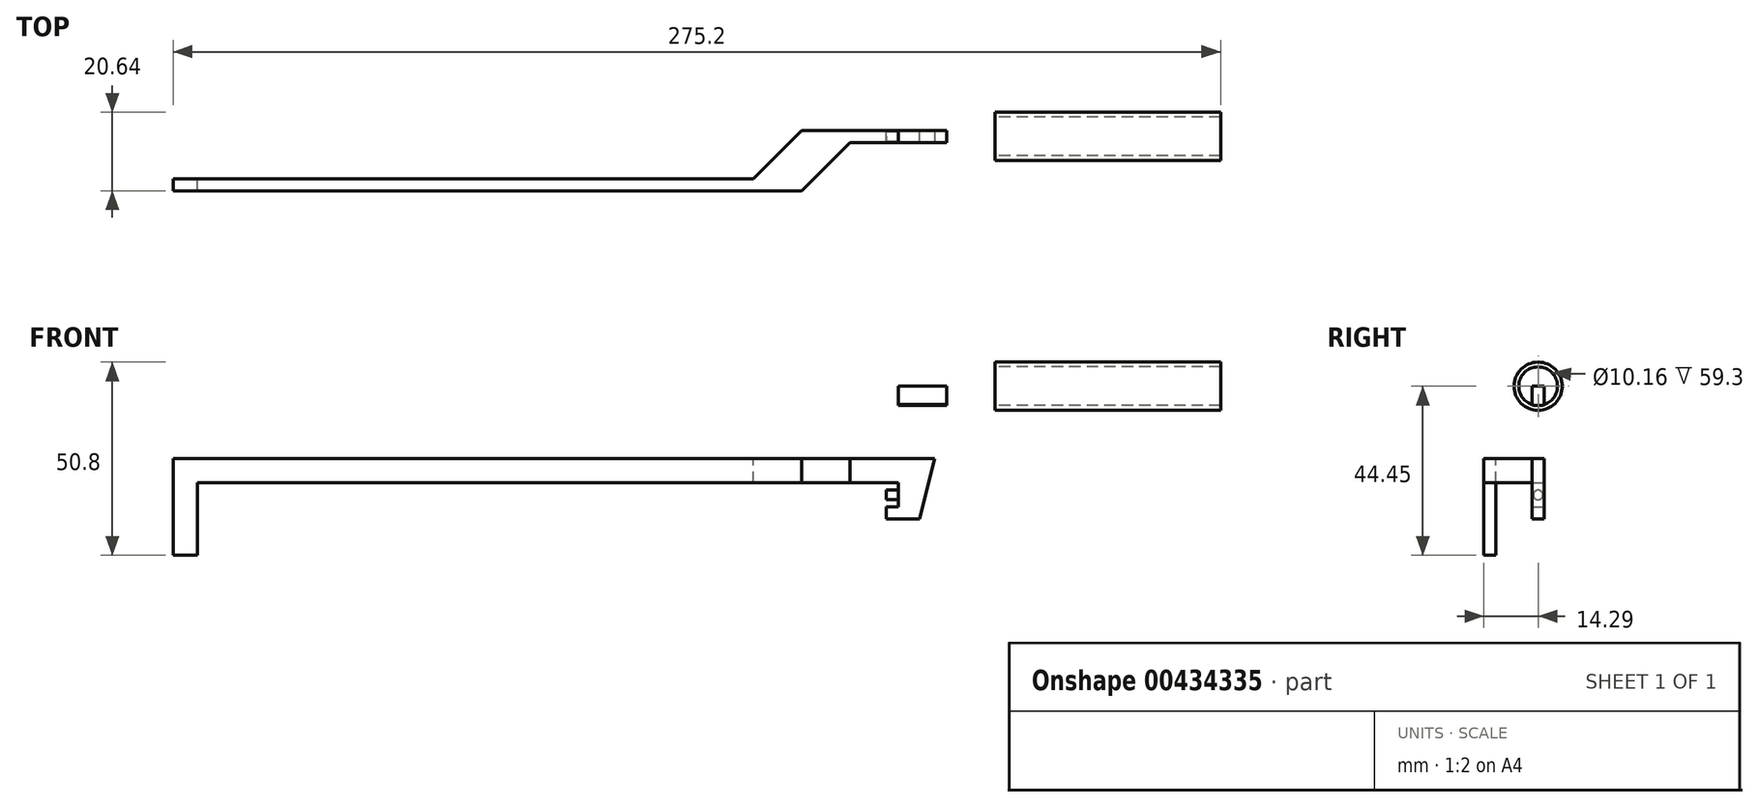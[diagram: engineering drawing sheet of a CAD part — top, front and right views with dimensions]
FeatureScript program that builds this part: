
annotation { "Feature Type Name" : "Feature", "Feature Type Description" : "" }
export const myFeature = defineFeature(function(context is Context, id is Id, definition is map)
    precondition{}
    {
        {
            var Q0;
            Q0=qCreatedBy(makeId("Right.planeOp"),FACE);
            var sketch = newSketch(context, id + "F0", { "sketchPlane" : qUnion([Q0])});
            skCircle(sketch, "E0", {"center": v(0, 0) * mm, "radius": 6.35 * mm});
            skCircle(sketch, "E1", {"center": v(0, 0) * mm, "radius": 5.08 * mm});
            skSolve(sketch);
        }
        {
            var Q0;
            Q0=makeQuery(id+"F0.imprint","IMPRINT",FACE,{"disambiguationData":[TD([[makeQuery(id+"F0.imprint","IMPRINT",EDGE,{"derivedFrom":sQuery(id+"F0.wireOp",EDGE,"E0")}),1.0]])]});
            extrude(context, id + "F1", {"entities" : qUnion([Q0]), "depth" : 72 * mm + 12.7 * mm});
        }
        {
            var Q0;
            Q0=qCreatedBy(makeId("Front.planeOp"),FACE);
            var sketch = newSketch(context, id + "F2", { "sketchPlane" : qUnion([Q0])});
            skLineSegment(sketch, "E2", {"start": v(36, 0) * mm, "end": v(0, 0) * mm});
            skLineSegment(sketch, "E3", {"start": v(0, 0) * mm, "end": v(0, -6.35) * mm});
            skLineSegment(sketch, "E4", {"start": v(12.7, -6.35) * mm, "end": v(12.7, 0) * mm});
            skLineSegment(sketch, "E5", {"start": v(0, -6.35) * mm, "end": v(0, -19.05) * mm});
            skLineSegment(sketch, "E6", {"start": v(0, -19.05) * mm, "end": v(-190.5, -19.05) * mm});
            skLineSegment(sketch, "E7", {"start": v(0, -19.05) * mm, "end": v(9.53, -19.05) * mm});
            skLineSegment(sketch, "E8", {"start": v(9.53, -19.05) * mm, "end": v(12.7, -6.35) * mm});
            skLineSegment(sketch, "E9", {"start": v(-190.5, -19.05) * mm, "end": v(-190.5, -44.45) * mm});
            skLineSegment(sketch, "E10", {"start": v(-190.5, -44.45) * mm, "end": v(-184.15, -44.45) * mm});
            skLineSegment(sketch, "E11", {"start": v(0, -19.05) * mm, "end": v(0, -25.4) * mm});
            skLineSegment(sketch, "E12", {"start": v(0, -25.4) * mm, "end": v(-190.5, -25.4) * mm});
            skLineSegment(sketch, "E13", {"start": v(9.53, -19.05) * mm, "end": v(7.94, -25.4) * mm});
            skLineSegment(sketch, "E14", {"start": v(0, -25.4) * mm, "end": v(7.94, -25.4) * mm});
            skPoint(sketch, "E15", {"position": v(-187.33, -25.4) * mm});
            skLineSegment(sketch, "E16", {"start": v(-184.15, -44.45) * mm, "end": v(-184.15, -41.28) * mm});
            skPoint(sketch, "E17", {"position": v(-187.33, -38.1) * mm});
            skArc(sketch, "E18", {"start": v(-187.33, -25.4) * mm, "mid": v(-186.52, -33.5) * mm, "end": v(-184.15, -41.28) * mm});
            skLineSegment(sketch, "E19", {"start": v(0, -25.4) * mm, "end": v(0, -31.75) * mm});
            skLineSegment(sketch, "E20", {"start": v(7.94, -25.4) * mm, "end": v(5.56, -34.92) * mm});
            skLineSegment(sketch, "E21", {"start": v(0, -31.75) * mm, "end": v(6.35, -31.75) * mm});
            skLineSegment(sketch, "E22", {"start": v(0, -31.75) * mm, "end": v(0, -34.92) * mm});
            skLineSegment(sketch, "E23", {"start": v(0, -34.92) * mm, "end": v(5.56, -34.92) * mm});
            skLineSegment(sketch, "E24", {"start": v(0, -34.92) * mm, "end": v(-3.17, -34.92) * mm});
            skLineSegment(sketch, "E25", {"start": v(-3.17, -34.92) * mm, "end": v(-3.17, -31.75) * mm});
            skLineSegment(sketch, "E26", {"start": v(-3.17, -31.75) * mm, "end": v(0, -31.75) * mm});
            skLineSegment(sketch, "E27", {"start": v(-184.15, -41.28) * mm, "end": v(-184.15, -25.4) * mm});
            skSolve(sketch);
        }
        {
            var Q0;
            {var subQ4=sQuery(id+"F2.wireOp",EDGE,"E6");Q0=makeQuery(id+"F2.imprint","IMPRINT",FACE,{"disambiguationData":[TD([[makeQuery(id+"F2.imprint","IMPRINT",EDGE,{"derivedFrom":subQ4}),1.0]])]});}
            var Q1;
            Q1=makeQuery(id+"F2.imprint","IMPRINT",FACE,{"disambiguationData":[TD([[makeQuery(id+"F2.imprint","IMPRINT",EDGE,{"derivedFrom":sQuery(id+"F2.wireOp",EDGE,"E7")}),-1.0]])]});
            var Q2;
            {var subQ1=sQuery(id+"F2.wireOp",EDGE,"E3");Q2=makeQuery(id+"F2.imprint","IMPRINT",FACE,{"disambiguationData":[TD([[makeQuery(id+"F2.imprint","IMPRINT",EDGE,{"derivedFrom":subQ1}),1.0]])]});}
            var Q3;
            {var subQ0=sQuery(id+"F2.wireOp",EDGE,"E14");Q3=makeQuery(id+"F2.imprint","IMPRINT",FACE,{"disambiguationData":[TD([[makeQuery(id+"F2.imprint","IMPRINT",EDGE,{"derivedFrom":subQ0}),-1.0]])]});}
            var Q4;
            {var subQ2=sQuery(id+"F2.wireOp",EDGE,"E21");Q4=makeQuery(id+"F2.imprint","IMPRINT",FACE,{"disambiguationData":[TD([[makeQuery(id+"F2.imprint","IMPRINT",EDGE,{"derivedFrom":subQ2}),-1.0]])]});}
            var Q5;
            Q5=makeQuery(id+"F2.imprint","IMPRINT",FACE,{"disambiguationData":[TD([[makeQuery(id+"F2.imprint","IMPRINT",EDGE,{"derivedFrom":sQuery(id+"F2.wireOp",EDGE,"E22")}),-1.0]])]});
            var Q6;
            {var subQ0=sQuery(id+"F2.wireOp",EDGE,"E10");Q6=makeQuery(id+"F2.imprint","IMPRINT",FACE,{"disambiguationData":[TD([[makeQuery(id+"F2.imprint","IMPRINT",EDGE,{"derivedFrom":subQ0}),1.0]])]});}
            var Q7;
            {var subQ0=sQuery(id+"F2.wireOp",EDGE,"E18");Q7=makeQuery(id+"F2.imprint","IMPRINT",FACE,{"disambiguationData":[TD([[makeQuery(id+"F2.imprint","IMPRINT",EDGE,{"derivedFrom":subQ0}),1.0]])]});}
            extrude(context, id + "F3", {"entities" : qUnion([Q0, Q1, Q2, Q3, Q4, Q5, Q6, Q7]), "operationType" : NewBodyOperationType.ADD, "endBound" : BoundingType.SYMMETRIC, "depth" : 3.17 * mm});
        }
        {
            var Q0;
            Q0=makeQuery(id+"F3.boolean.opBoolean","MERGE",FACE,{"derivedFrom":[makeQuery(id+"F1.opExtrude","CAP_FACE",FACE,{"disambiguationData":[OSD([sQuery(id+"F0.wireOp",EDGE,"E0"),sQuery(id+"F0.wireOp",EDGE,"E1")])],"isStart":true}),makeQuery(id+"F3.opExtrude","SWEPT_FACE",FACE,{"disambiguationData":[OSD([sQuery(id+"F2.wireOp",EDGE,"E3"),sQuery(id+"F2.wireOp",EDGE,"E5")])]})]});
            var sketch = newSketch(context, id + "F4", { "sketchPlane" : qUnion([Q0])});
            skCircle(sketch, "E28", {"center": v(0, 0) * mm, "radius": 5.08 * mm});
            skSolve(sketch);
        }
        {
            var Q0;
            Q0=makeQuery(id+"F4.imprint","IMPRINT",FACE,{"disambiguationData":[TD([[makeQuery(id+"F4.imprint","IMPRINT",EDGE,{"disambiguationData":[OD(1.0)],"derivedFrom":sQuery(id+"F4.wireOp",EDGE,"E28")}),-1.0]])]});
            var Q1;
            Q1=makeQuery(id+"F4.imprint","IMPRINT",FACE,{"disambiguationData":[TD([[makeQuery(id+"F4.imprint","IMPRINT",EDGE,{"disambiguationData":[OD(0.0)],"derivedFrom":sQuery(id+"F4.wireOp",EDGE,"E28")}),1.0]])]});
            extrude(context, id + "F5", {"entities" : qUnion([Q0, Q1]), "operationType" : NewBodyOperationType.REMOVE, "oppositeDirection" : true, "depth" : 25.4 * mm});
        }
        {
            var Q0;
            Q0=makeQuery(id+"F3.opExtrude","SWEPT_FACE",FACE,{"disambiguationData":[OSD([sQuery(id+"F2.wireOp",EDGE,"E19")])]});
            var sketch = newSketch(context, id + "F6", { "sketchPlane" : qUnion([Q0])});
            skPoint(sketch, "E29", {"position": v(0, -28.57) * mm});
            skCircle(sketch, "E30", {"center": v(0, -28.57) * mm, "radius": 1.27 * mm});
            skSolve(sketch);
        }
        {
            var Q0;
            Q0=makeQuery(id+"F6.imprint","IMPRINT",FACE,{"disambiguationData":[TD([[makeQuery(id+"F6.imprint","IMPRINT",EDGE,{"derivedFrom":sQuery(id+"F6.wireOp",EDGE,"E30")}),1.0]])]});
            extrude(context, id + "F7", {"entities" : qUnion([Q0]), "operationType" : NewBodyOperationType.ADD, "depth" : 3.17 * mm});
        }
        {
            var Q0;
            {var subQ0=sQuery(id+"F2.wireOp",EDGE,"E12");var subQ1=sQuery(id+"F2.wireOp",EDGE,"E10");var subQ2=sQuery(id+"F2.wireOp",EDGE,"E9");var subQ3=sQuery(id+"F2.wireOp",EDGE,"E20");var subQ4=sQuery(id+"F2.wireOp",EDGE,"E13");var subQ5=sQuery(id+"F2.wireOp",EDGE,"E8");var subQ6=sQuery(id+"F2.wireOp",EDGE,"E6");var subQ7=sQuery(id+"F2.wireOp",EDGE,"E27");var subQ8=sQuery(id+"F2.wireOp",EDGE,"E16");var subQ9=sQuery(id+"F0.wireOp",EDGE,"E0");var subQ10=sQuery(id+"F2.wireOp",EDGE,"E5");var subQ11=sQuery(id+"F2.wireOp",EDGE,"E3");var subQ12=sQuery(id+"F2.wireOp",EDGE,"E4");var subQ13=sQuery(id+"F2.wireOp",EDGE,"E19");var subQ14=sQuery(id+"F2.wireOp",EDGE,"E24");var subQ15=sQuery(id+"F2.wireOp",EDGE,"E23");var subQ16=sQuery(id+"F2.wireOp",EDGE,"E25");var subQ17=sQuery(id+"F2.wireOp",EDGE,"E26");Q0=makeQuery(id+"F3.boolean.opBoolean","SPLIT",FACE,{"disambiguationData":[TD([makeQuery(id+"F1.opExtrude","SWEPT_FACE",FACE,{"disambiguationData":[OSD([subQ9])]})])],"derivedFrom":makeQuery(id+"F3.opExtrude","CAP_FACE",FACE,{"disambiguationData":[OSD([sQuery(id+"F2.wireOp",EDGE,"E2"),subQ11,subQ12,subQ10,subQ6,subQ5,subQ2,subQ1,subQ0,subQ4,subQ8,subQ13,subQ3,subQ15,subQ14,subQ16,subQ17,subQ7])],"isStart":false})});}
            var sketch = newSketch(context, id + "F8", { "sketchPlane" : qUnion([Q0])});
            skLineSegment(sketch, "E31.bottom", {"start": v(-190.5, -19.05) * mm, "end": v(-184.15, -19.05) * mm});
            skLineSegment(sketch, "E31.top", {"start": v(-190.5, -44.45) * mm, "end": v(-184.15, -44.45) * mm});
            skLineSegment(sketch, "E31.left", {"start": v(-190.5, -19.05) * mm, "end": v(-190.5, -44.45) * mm});
            skLineSegment(sketch, "E31.right", {"start": v(-184.15, -25.4) * mm, "end": v(-184.15, -44.45) * mm});
            skLineSegment(sketch, "E32.bottom", {"start": v(-184.15, -19.05) * mm, "end": v(0, -19.05) * mm});
            skLineSegment(sketch, "E32.top", {"start": v(-184.15, -25.4) * mm, "end": v(0, -25.4) * mm});
            skLineSegment(sketch, "E32.right", {"start": v(0, -19.05) * mm, "end": v(0, -25.4) * mm});
            skSolve(sketch);
        }
        {
            var Q0;
            Q0=makeQuery(id+"F8.imprint","IMPRINT",FACE,{"disambiguationData":[TD([[makeQuery(id+"F8.imprint","IMPRINT",EDGE,{"derivedFrom":sQuery(id+"F8.wireOp",EDGE,"E31.bottom")}),1.0]])]});
            extrude(context, id + "F9", {"entities" : qUnion([Q0]), "operationType" : NewBodyOperationType.ADD, "depth" : 12.7 * mm});
        }
        {
            var Q0;
            Q0=makeQuery(id+"F9.boolean.opBoolean","MERGE",FACE,{"derivedFrom":[makeQuery(id+"F3.opExtrude","SWEPT_FACE",FACE,{"disambiguationData":[OSD([sQuery(id+"F2.wireOp",EDGE,"E6")])]}),makeQuery(id+"F9.opExtrude","SWEPT_FACE",FACE,{"disambiguationData":[OSD([sQuery(id+"F8.wireOp",EDGE,"E31.bottom"),sQuery(id+"F8.wireOp",EDGE,"E32.bottom")])]})]});
            var sketch = newSketch(context, id + "F10", { "sketchPlane" : qUnion([Q0])});
            skLineSegment(sketch, "E33.bottom", {"start": v(-190.5, -14.29) * mm, "end": v(-25.4, -14.29) * mm});
            skLineSegment(sketch, "E33.top", {"start": v(-190.5, -11.11) * mm, "end": v(-25.4, -11.11) * mm});
            skLineSegment(sketch, "E33.left", {"start": v(-190.5, -14.29) * mm, "end": v(-190.5, -11.11) * mm});
            skLineSegment(sketch, "E33.right", {"start": v(-25.4, -14.29) * mm, "end": v(-25.4, -11.11) * mm});
            skLineSegment(sketch, "E34.bottom", {"start": v(0, 1.59) * mm, "end": v(-25.4, 1.59) * mm});
            skLineSegment(sketch, "E34.top", {"start": v(0, -1.59) * mm, "end": v(-25.4, -1.59) * mm});
            skLineSegment(sketch, "E34.left", {"start": v(0, 1.59) * mm, "end": v(0, -1.59) * mm});
            skLineSegment(sketch, "E34.right", {"start": v(-25.4, 1.59) * mm, "end": v(-25.4, -1.59) * mm});
            skLineSegment(sketch, "E35", {"start": v(-25.4, -14.29) * mm, "end": v(0, -14.29) * mm});
            skLineSegment(sketch, "E36", {"start": v(0, -14.29) * mm, "end": v(0, -1.59) * mm});
            skLineSegment(sketch, "E37", {"start": v(-25.4, 1.59) * mm, "end": v(-190.5, 1.59) * mm});
            skLineSegment(sketch, "E38", {"start": v(-190.5, 1.59) * mm, "end": v(-190.5, -11.11) * mm});
            skLineSegment(sketch, "E39", {"start": v(-25.4, -14.29) * mm, "end": v(-12.7, -1.59) * mm});
            skLineSegment(sketch, "E40", {"start": v(-25.4, 1.59) * mm, "end": v(-38.1, -11.11) * mm});
            skSolve(sketch);
        }
        {
            var Q0;
            Q0=makeQuery(id+"F10.imprint","IMPRINT",FACE,{"disambiguationData":[TD([[makeQuery(id+"F10.imprint","IMPRINT",EDGE,{"derivedFrom":sQuery(id+"F10.wireOp",EDGE,"E33.top")}),1.0]])]});
            var Q1;
            {var subQ2=sQuery(id+"F10.wireOp",EDGE,"qEK2lggY-Jh6i-ebW2-eIzc-xvW6Pxc006k9");Q1=makeQuery(id+"F10.imprint","IMPRINT",FACE,{"disambiguationData":[TD([[makeQuery(id+"F10.imprint","IMPRINT",EDGE,{"derivedFrom":subQ2}),-1.0]])]});}
            var Q2;
            Q2=makeQuery(id+"F10.imprint","IMPRINT",FACE,{"disambiguationData":[TD([[makeQuery(id+"F10.imprint","IMPRINT",EDGE,{"derivedFrom":sQuery(id+"F10.wireOp",EDGE,"E35")}),-1.0]])]});
            extrude(context, id + "F11", {"entities" : qUnion([Q0, Q1, Q2]), "operationType" : NewBodyOperationType.REMOVE, "oppositeDirection" : true, "depth" : 127 * mm});
        }
    });
